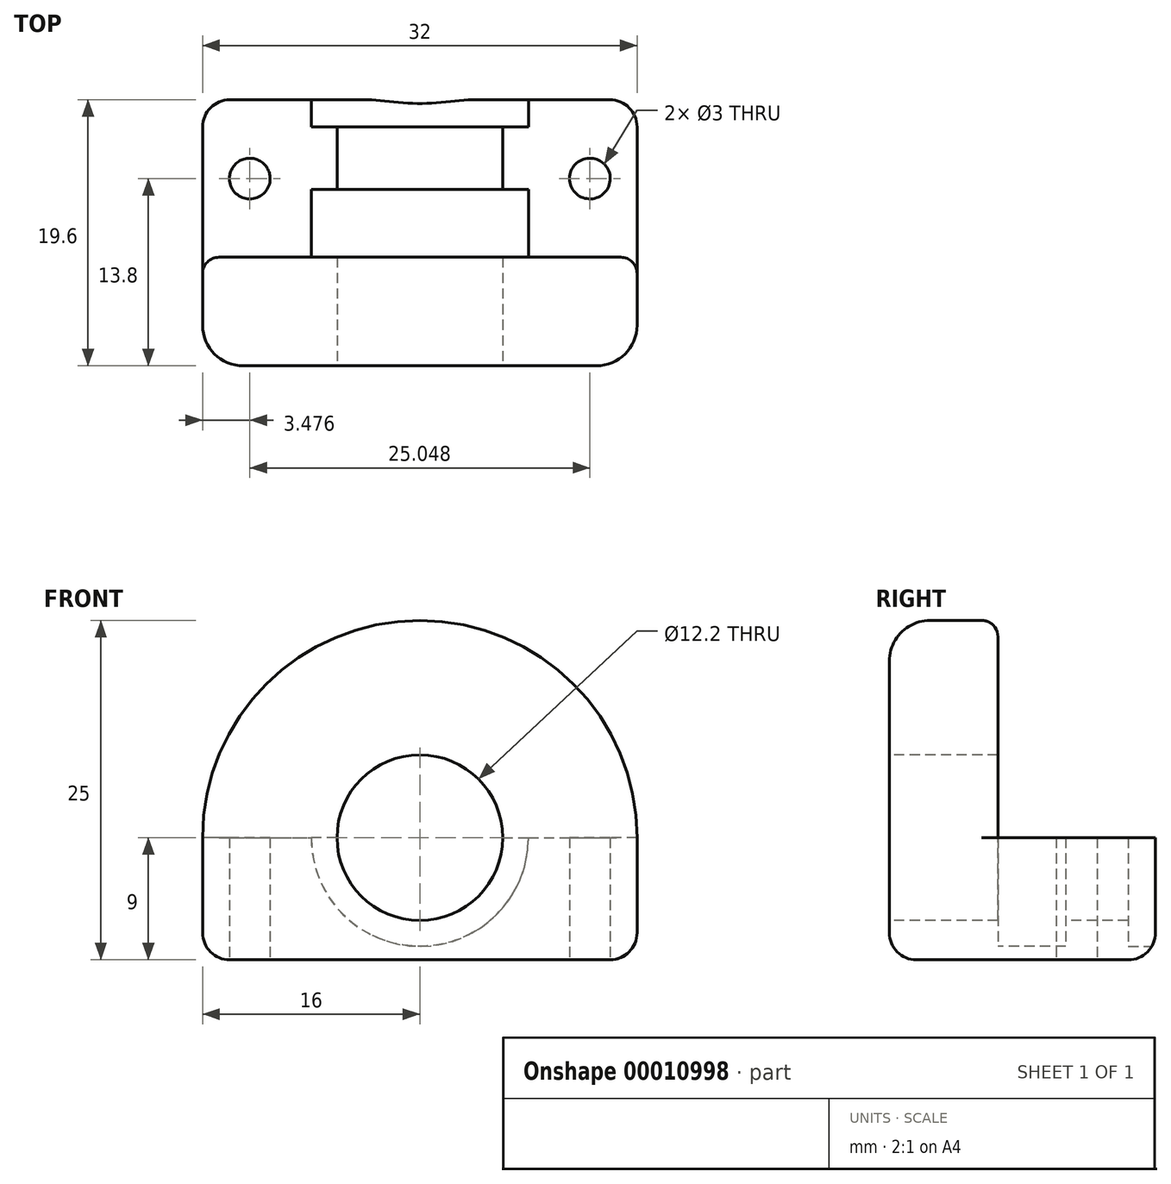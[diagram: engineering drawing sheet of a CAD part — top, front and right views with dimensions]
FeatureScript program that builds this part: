
annotation { "Feature Type Name" : "Feature", "Feature Type Description" : "" }
export const myFeature = defineFeature(function(context is Context, id is Id, definition is map)
    precondition{}
    {
        {
            var Q0;
            Q0=qCreatedBy(makeId("Top.planeOp"),FACE);
            var sketch = newSketch(context, id + "F0", { "sketchPlane" : qUnion([Q0])});
            skLineSegment(sketch, "E0.rect.bottom", {"start": v(-16, 5.8) * mm, "end": v(16, 5.8) * mm});
            skLineSegment(sketch, "E0.rect.top", {"start": v(-16, -5.8) * mm, "end": v(16, -5.8) * mm});
            skLineSegment(sketch, "E0.rect.left", {"start": v(-16, 5.8) * mm, "end": v(-16, -5.8) * mm});
            skLineSegment(sketch, "E0.rect.right", {"start": v(16, 5.8) * mm, "end": v(16, -5.8) * mm});
            skPoint(sketch, "E0.rect.middle", {"position": v(0, 0) * mm});
            skCircle(sketch, "E1", {"center": v(12.52, 0) * mm, "radius": 1.5 * mm});
            skCircle(sketch, "E2", {"center": v(-12.52, 0) * mm, "radius": 1.5 * mm});
            skSolve(sketch);
        }
        {
            var Q0;
            Q0=makeQuery(id+"F0.imprint","IMPRINT",FACE,{"disambiguationData":[TD([[makeQuery(id+"F0.imprint","IMPRINT",EDGE,{"derivedFrom":sQuery(id+"F0.wireOp",EDGE,"E0.rect.bottom")}),-1.0]])]});
            extrude(context, id + "F1", {"entities" : qUnion([Q0]), "depth" : 9 * mm});
        }
        {
            var Q0;
            Q0=makeQuery(id+"F1.opExtrude","SWEPT_FACE",FACE,{"disambiguationData":[OSD([sQuery(id+"F0.wireOp",EDGE,"E0.rect.top")])]});
            var sketch = newSketch(context, id + "F2", { "sketchPlane" : qUnion([Q0])});
            skCircle(sketch, "E3", {"center": v(0, 9) * mm, "radius": 8 * mm});
            skSolve(sketch);
        }
        {
            var Q0;
            Q0=qSketchRegion(id+"F2",true);
            var Q1;
            Q1=makeQuery(id+"F1.opExtrude","SWEPT_FACE",FACE,{"disambiguationData":[OSD([sQuery(id+"F0.wireOp",EDGE,"E0.rect.bottom")])]});
            extrude(context, id + "F3", {"entities" : qUnion([Q0, Q1]), "operationType" : NewBodyOperationType.REMOVE, "oppositeDirection" : true, "depth" : 5 * mm});
        }
        {
            var Q0;
            Q0=makeQuery(id+"F1.opExtrude","SWEPT_FACE",FACE,{"disambiguationData":[OSD([sQuery(id+"F0.wireOp",EDGE,"E0.rect.bottom")])]});
            var sketch = newSketch(context, id + "F4", { "sketchPlane" : qUnion([Q0])});
            skCircle(sketch, "E4", {"center": v(0, 9) * mm, "radius": 8 * mm});
            skSolve(sketch);
        }
        {
            var Q0;
            Q0=qSketchRegion(id+"F4",true);
            extrude(context, id + "F5", {"entities" : qUnion([Q0]), "operationType" : NewBodyOperationType.REMOVE, "oppositeDirection" : true, "depth" : 2 * mm});
        }
        {
            var Q0;
            Q0=makeQuery(id+"F5.boolean.opBoolean","COPY",FACE,{"derivedFrom":makeQuery(id+"F5.opExtrude","CAP_FACE",FACE,{"disambiguationData":[OSD([sQuery(id+"F4.wireOp",EDGE,"E4")])],"isStart":false})});
            var sketch = newSketch(context, id + "F6", { "sketchPlane" : qUnion([Q0])});
            skCircle(sketch, "E5", {"center": v(0, 9) * mm, "radius": 6 * mm});
            skSolve(sketch);
        }
        {
            var Q0;
            Q0=qSketchRegion(id+"F6",true);
            extrude(context, id + "F7", {"entities" : qUnion([Q0]), "operationType" : NewBodyOperationType.REMOVE, "oppositeDirection" : true, "depth" : 25 * mm});
        }
        {
            var Q0;
            Q0=makeQuery(id+"F1.opExtrude","CAP_EDGE",EDGE,{"disambiguationData":[OSD([sQuery(id+"F0.wireOp",EDGE,"E0.rect.bottom")])],"isStart":true});
            var Q1;
            Q1=makeQuery(id+"F7.boolean.opBoolean","COPY",EDGE,{"derivedFrom":makeQuery(id+"F7.opExtrude","CAP_EDGE",EDGE,{"disambiguationData":[OSD([sQuery(id+"F6.wireOp",EDGE,"E5")])],"isStart":true})});
            var Q2;
            Q2=makeQuery(id+"F1.opExtrude","SWEPT_EDGE",EDGE,{"disambiguationData":[OSD([sQuery(id+"F0.wireOp",EDGE,"E0.rect.bottom"),sQuery(id+"F0.wireOp",EDGE,"E0.rect.left")])]});
            var Q3;
            Q3=makeQuery(id+"F1.opExtrude","CAP_EDGE",EDGE,{"disambiguationData":[OSD([sQuery(id+"F0.wireOp",EDGE,"E0.rect.left")])],"isStart":true});
            var Q4;
            Q4=makeQuery(id+"F1.opExtrude","CAP_EDGE",EDGE,{"disambiguationData":[OSD([sQuery(id+"F0.wireOp",EDGE,"E0.rect.right")])],"isStart":true});
            var Q5;
            Q5=makeQuery(id+"F1.opExtrude","SWEPT_EDGE",EDGE,{"disambiguationData":[OSD([sQuery(id+"F0.wireOp",EDGE,"E0.rect.bottom"),sQuery(id+"F0.wireOp",EDGE,"E0.rect.right")])]});
            fillet(context, id + "F8", {"entities" : qUnion([Q0, Q1, Q2, Q3, Q4, Q5]), "radius" : 2 * mm, "tangentPropagation" : true, "allowEdgeOverflow" : false});
        }
        {
            var Q0;
            Q0=makeQuery(id+"F1.opExtrude","SWEPT_FACE",FACE,{"disambiguationData":[OSD([sQuery(id+"F0.wireOp",EDGE,"E0.rect.top")])]});
            var sketch = newSketch(context, id + "F9", { "sketchPlane" : qUnion([Q0])});
            skArc(sketch, "E6", {"start": v(16, 9) * mm, "mid": v(0, 25) * mm, "end": v(-16, 9) * mm});
            skLineSegment(sketch, "E7", {"start": v(0, 0) * mm, "end": v(13.23, 0) * mm});
            skLineSegment(sketch, "E8", {"start": v(-13.23, 0) * mm, "end": v(0, 0) * mm});
            skLineSegment(sketch, "E9", {"start": v(-16, 9) * mm, "end": v(-16, 0) * mm});
            skLineSegment(sketch, "E10", {"start": v(16, 9) * mm, "end": v(16, 0) * mm});
            skLineSegment(sketch, "E11", {"start": v(-16, 0) * mm, "end": v(16, 0) * mm});
            skSolve(sketch);
        }
        {
            var Q0;
            Q0=qSketchRegion(id+"F9",true);
            extrude(context, id + "F10", {"entities" : qUnion([Q0]), "operationType" : NewBodyOperationType.ADD, "depth" : 8 * mm});
        }
        {
            var Q0;
            Q0=makeQuery(id+"F10.opExtrude","CAP_EDGE",EDGE,{"disambiguationData":[OSD([sQuery(id+"F9.wireOp",EDGE,"E6")])],"isStart":false});
            fillet(context, id + "F11", {"entities" : qUnion([Q0]), "radius" : 3 * mm, "tangentPropagation" : true, "allowEdgeOverflow" : false});
        }
        {
            var Q0;
            Q0=makeQuery(id+"F10.opExtrude","CAP_EDGE",EDGE,{"disambiguationData":[OSD([sQuery(id+"F9.wireOp",EDGE,"E6")])],"isStart":true});
            fillet(context, id + "F12", {"entities" : qUnion([Q0]), "radius" : 1.2 * mm, "tangentPropagation" : true, "allowEdgeOverflow" : false});
        }
        {
            var Q0;
            Q0=makeQuery(id+"F10.opExtrude","CAP_FACE",FACE,{"disambiguationData":[OSD([sQuery(id+"F9.wireOp",EDGE,"E6"),sQuery(id+"F9.wireOp",EDGE,"E9"),sQuery(id+"F9.wireOp",EDGE,"E10"),sQuery(id+"F9.wireOp",EDGE,"E11")])],"isStart":false});
            var sketch = newSketch(context, id + "F13", { "sketchPlane" : qUnion([Q0])});
            skCircle(sketch, "E12", {"center": v(0, 9) * mm, "radius": 6.1 * mm});
            skSolve(sketch);
        }
        {
            var Q0;
            Q0=qSketchRegion(id+"F13",true);
            extrude(context, id + "F14", {"entities" : qUnion([Q0]), "operationType" : NewBodyOperationType.REMOVE, "endBound" : BoundingType.THROUGH_ALL, "oppositeDirection" : true, "depth" : 25 * mm});
        }
        {
            var Q0;
            Q0=makeQuery(id+"F11.opFillet","BLEND_EDGE",EDGE,{"blendedFrom":[makeQuery(id+"F10.opExtrude","CAP_EDGE",EDGE,{"disambiguationData":[OSD([sQuery(id+"F9.wireOp",EDGE,"E9")])],"isStart":false}),makeQuery(id+"F10.boolean.opBoolean","MERGE",FACE,{"derivedFrom":[makeQuery(id+"F1.opExtrude","CAP_FACE",FACE,{"disambiguationData":[OSD([sQuery(id+"F0.wireOp",EDGE,"E0.rect.bottom"),sQuery(id+"F0.wireOp",EDGE,"E0.rect.top"),sQuery(id+"F0.wireOp",EDGE,"E0.rect.left"),sQuery(id+"F0.wireOp",EDGE,"E0.rect.right"),sQuery(id+"F0.wireOp",EDGE,"E1"),sQuery(id+"F0.wireOp",EDGE,"E2")])],"isStart":true}),makeQuery(id+"F10.opExtrude","SWEPT_FACE",FACE,{"disambiguationData":[OSD([sQuery(id+"F9.wireOp",EDGE,"E11")])]})]})],"blendedInto":[makeQuery(id+"F10.boolean.opBoolean","MERGE",FACE,{"derivedFrom":[makeQuery(id+"F1.opExtrude","CAP_FACE",FACE,{"disambiguationData":[OSD([sQuery(id+"F0.wireOp",EDGE,"E0.rect.bottom"),sQuery(id+"F0.wireOp",EDGE,"E0.rect.top"),sQuery(id+"F0.wireOp",EDGE,"E0.rect.left"),sQuery(id+"F0.wireOp",EDGE,"E0.rect.right"),sQuery(id+"F0.wireOp",EDGE,"E1"),sQuery(id+"F0.wireOp",EDGE,"E2")])],"isStart":true}),makeQuery(id+"F10.opExtrude","SWEPT_FACE",FACE,{"disambiguationData":[OSD([sQuery(id+"F9.wireOp",EDGE,"E11")])]})]})]});
            fillet(context, id + "F15", {"entities" : qUnion([Q0]), "radius" : 2 * mm, "tangentPropagation" : true, "allowEdgeOverflow" : false});
        }
    });
